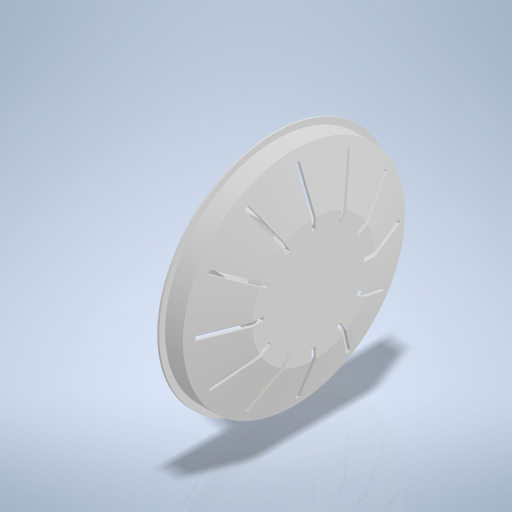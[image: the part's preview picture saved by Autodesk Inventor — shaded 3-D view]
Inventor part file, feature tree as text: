
AUTODESK INVENTOR PART (.ipt)
format: ipt  version: 2024 (Build 280153000, 153)  size: 856,576 bytes
history: native  units: mm
features: sketch x8, plane x6, extrude x3, projected_geometry x3, revolve x2, fillet x2, sweep x1, pattern_circular x1
ambient origin geometry x8: Origin, YZ Plane, XZ Plane, XY Plane, X Axis, Y Axis, Z Axis, Center Point
bodies: Body1 (feature_tree)
feature tree (26):
  revolve  "Umdrehung4"
  extrude  "Extrusion1"  Depth=30.0mm
  fillet  "Rundung1"  Radius=5.0mm
  plane  "Arbeitsebene1"
  extrude  "Extrusion4"  Depth=150.0mm
  extrude  "Extrusion5"  Depth=100.0mm
  plane  "Arbeitsebene4"
  revolve  "Umdrehung5"
  plane  "Arbeitsebene5"
  plane  "Arbeitsebene7"
  sketch  "Skizze10"  dims[d45=0.0mm]
  plane  "Arbeitsebene8"
  plane  "Arbeitsebene9"
  sweep  "Sweeping3"
  pattern_circular  "Runde Anordnung3"  Count=5  [1 undecoded]
  fillet  "Rundung2"  Radius=20.0mm
  sketch  "Skizze1"  dims[d1=20.0mm d2=30.0mm d5=5.0mm]
  sketch  "Skizze2"  dims[d6=5.0mm d7=150.0mm]
  sketch  "Skizze3"  dims[d8=50.0mm d10=100.0mm]
  projected_geometry  "Projizierte Kontur1"
  sketch  "Skizze6"  dims[d29=125.0mm d39=280.0mm]
  projected_geometry  "Projizierte Kontur2"
  sketch  "Skizze7"  dims[d41=90.0deg d42=50.0mm d43=0.0mm d44=20.0mm]
  projected_geometry  "Projizierte Kontur3"
  sketch  "Skizze13"  dims[d47=130.0mm]
  sketch  "Skizze14"  dims[d48=127.455056mm d49=10.0mm d61=120.0mm d63=360.0deg d73=10.0mm d74=0.0mm d75=230.0mm d76=0.0mm d77=0.0mm d78=230.0mm d80=360.0deg d81=-50.0mm d88=-60.0mm d89=30.0mm d90=0.0mm d96=125.0mm d97=500.0mm d98=-60.0mm d100=0.0mm d101=0.0mm d102=120.0mm d103=360.0deg d105=150.0mm d106=85.0mm d109=2.0mm]
note: 1 required parameter value undecoded (feature->parameter linkage not recoverable at this tier; creation-order binding heuristic only, values carry confidence <= 0.55)
